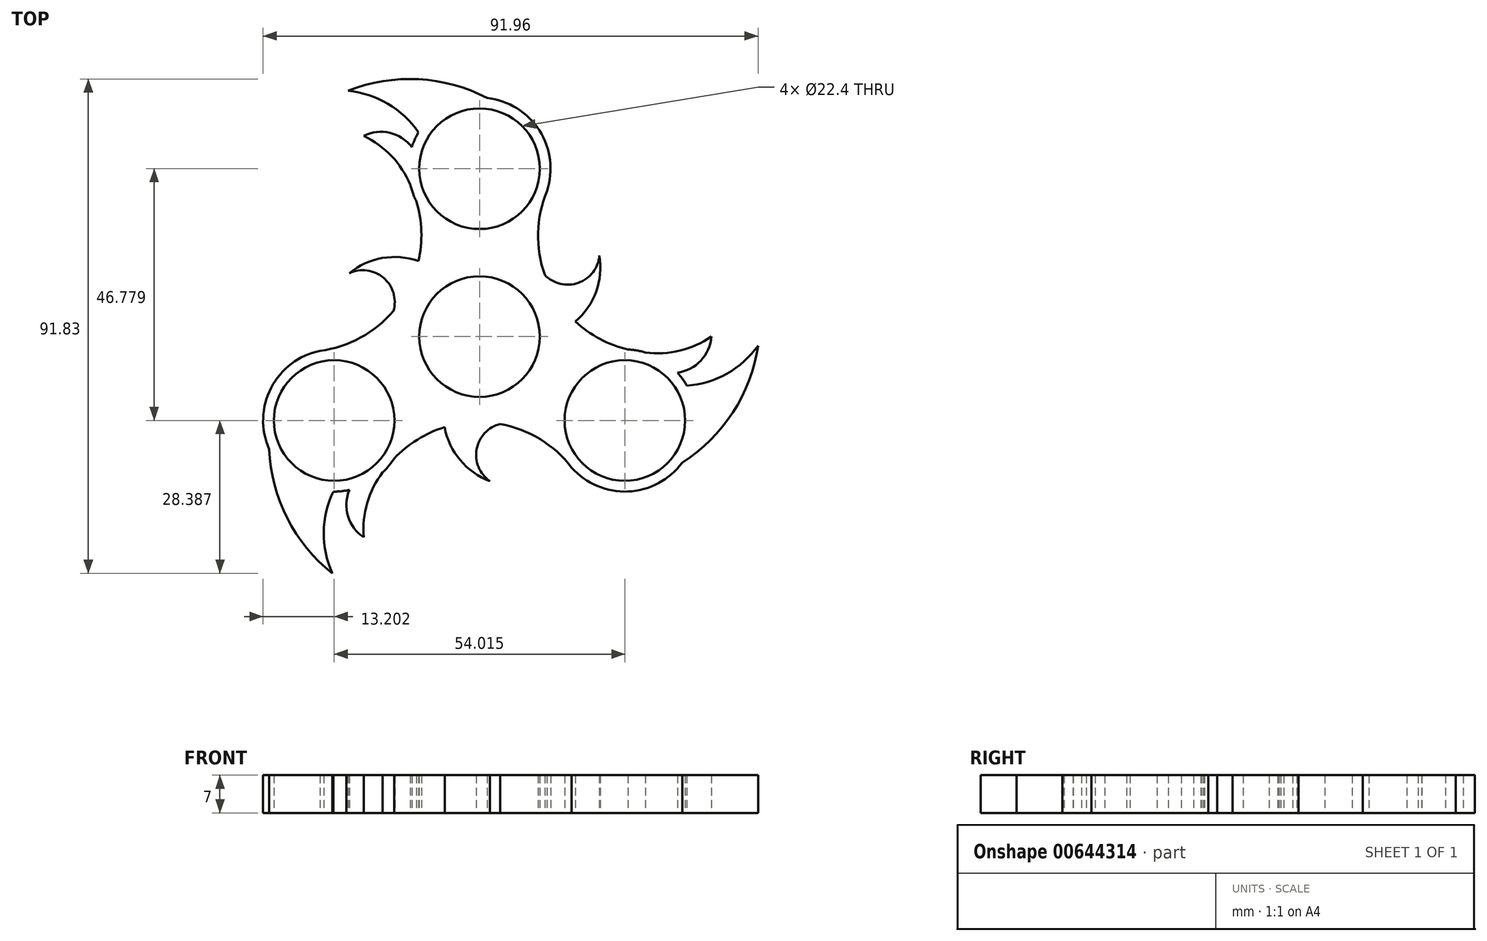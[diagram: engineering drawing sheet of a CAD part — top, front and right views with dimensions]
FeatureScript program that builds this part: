
annotation { "Feature Type Name" : "Feature", "Feature Type Description" : "" }
export const myFeature = defineFeature(function(context is Context, id is Id, definition is map)
    precondition{}
    {
        {
            var Q0;
            Q0=qCreatedBy(makeId("Top.planeOp"),FACE);
            var sketch = newSketch(context, id + "F0", { "sketchPlane" : qUnion([Q0])});
            skCircle(sketch, "E0", {"center": v(0, 0) * mm, "radius": 11.2 * mm});
            skCircle(sketch, "E1", {"center": v(0, 31.19) * mm, "radius": 11.2 * mm});
            skArc(sketch, "E2", {"start": v(12.11, 25.94) * mm, "mid": v(11.4, 37.82) * mm, "end": v(1.43, 44.3) * mm});
            skArc(sketch, "E3.1.0", {"start": v(-17.98, -25.22) * mm, "mid": v(-16.84, -24.01) * mm, "end": v(-15.87, -22.67) * mm});
            skCircle(sketch, "E3.1.1", {"center": v(-27, -15.6) * mm, "radius": 11.2 * mm});
            skArc(sketch, "E3.2.0", {"start": v(38.52, -9.13) * mm, "mid": v(37.71, -7.87) * mm, "end": v(36.77, -6.7) * mm});
            skCircle(sketch, "E3.2.1", {"center": v(27, -15.6) * mm, "radius": 11.2 * mm});
            skArc(sketch, "E4", {"start": v(37.66, -23.4) * mm, "mid": v(47.08, -14.08) * mm, "end": v(51.75, -1.68) * mm});
            skArc(sketch, "E5", {"start": v(38.52, -9.13) * mm, "mid": v(45.97, -6.88) * mm, "end": v(51.75, -1.68) * mm});
            skArc(sketch, "E6", {"start": v(36.77, -6.7) * mm, "mid": v(41.11, -4.48) * mm, "end": v(43.06, 0) * mm});
            skArc(sketch, "E7", {"start": v(30.84, -2.96) * mm, "mid": v(37.22, -2.6) * mm, "end": v(43.06, 0) * mm});
            skArc(sketch, "E8.1.0", {"start": v(1.43, 44.3) * mm, "mid": v(-11.35, 47.8) * mm, "end": v(-24.42, 45.66) * mm});
            skArc(sketch, "E8.2.0", {"start": v(-39.09, -20.92) * mm, "mid": v(-35.73, -33.73) * mm, "end": v(-27.33, -43.98) * mm});
            skArc(sketch, "E9.1.0", {"start": v(-11.35, 37.93) * mm, "mid": v(-17.03, 43.25) * mm, "end": v(-24.42, 45.66) * mm});
            skArc(sketch, "E9.1.2", {"start": v(-12.58, 35.2) * mm, "mid": v(-16.68, 37.84) * mm, "end": v(-21.53, 37.29) * mm});
            skArc(sketch, "E9.1.3", {"start": v(-12.85, 28.18) * mm, "mid": v(-16.35, 33.54) * mm, "end": v(-21.53, 37.29) * mm});
            skArc(sketch, "E9.2.0", {"start": v(-27.17, -28.8) * mm, "mid": v(-28.94, -36.37) * mm, "end": v(-27.33, -43.98) * mm});
            skArc(sketch, "E9.2.2", {"start": v(-24.19, -28.49) * mm, "mid": v(-24.43, -33.36) * mm, "end": v(-21.53, -37.29) * mm});
            skArc(sketch, "E9.2.3", {"start": v(-17.98, -25.22) * mm, "mid": v(-20.87, -30.93) * mm, "end": v(-21.53, -37.29) * mm});
            skArc(sketch, "E10", {"start": v(12.52, 27) * mm, "mid": v(10.88, 19.26) * mm, "end": v(12.12, 11.46) * mm});
            skArc(sketch, "E11.1.0", {"start": v(-29.64, -2.66) * mm, "mid": v(-22.12, -0.2) * mm, "end": v(-15.98, 4.77) * mm});
            skArc(sketch, "E11.2.0", {"start": v(17.12, -24.34) * mm, "mid": v(11.24, -19.06) * mm, "end": v(3.86, -16.23) * mm});
            skArc(sketch, "E12", {"start": v(12.12, 11.46) * mm, "mid": v(18.37, 9.98) * mm, "end": v(22.28, 15.07) * mm});
            skArc(sketch, "E13", {"start": v(17.81, 2.8) * mm, "mid": v(21.67, 8.35) * mm, "end": v(22.28, 15.07) * mm});
            skArc(sketch, "E14.1.0", {"start": v(-15.98, 4.77) * mm, "mid": v(-17.83, 10.92) * mm, "end": v(-24.2, 11.76) * mm});
            skArc(sketch, "E14.1.1", {"start": v(-11.34, 14.03) * mm, "mid": v(-18.06, 14.59) * mm, "end": v(-24.2, 11.76) * mm});
            skArc(sketch, "E14.2.0", {"start": v(3.86, -16.23) * mm, "mid": v(-0.54, -20.9) * mm, "end": v(1.91, -26.83) * mm});
            skArc(sketch, "E14.2.1", {"start": v(-6.48, -16.83) * mm, "mid": v(-3.6, -22.94) * mm, "end": v(1.91, -26.83) * mm});
            skArc(sketch, "E15.trimOffspring", {"start": v(-11.35, 37.93) * mm, "mid": v(-12.04, 36.6) * mm, "end": v(-12.58, 35.2) * mm});
            skArc(sketch, "E16.trimOffspring", {"start": v(-12.85, 28.18) * mm, "mid": v(-12.38, 26.6) * mm, "end": v(-11.7, 25.08) * mm});
            skArc(sketch, "E17.trimOffspring", {"start": v(-27.17, -28.8) * mm, "mid": v(-25.67, -28.72) * mm, "end": v(-24.19, -28.49) * mm});
            skArc(sketch, "E18.trimOffspring", {"start": v(30.84, -2.96) * mm, "mid": v(29.22, -2.58) * mm, "end": v(27.57, -2.4) * mm});
            skArc(sketch, "E19.trimOffspring", {"start": v(17.81, 2.8) * mm, "mid": v(22.35, -0.43) * mm, "end": v(27.57, -2.4) * mm});
            skArc(sketch, "E20.trimOffspring", {"start": v(-11.34, 14.03) * mm, "mid": v(-10.8, 19.57) * mm, "end": v(-11.7, 25.08) * mm});
            skArc(sketch, "E21.trimOffspring", {"start": v(-6.48, -16.83) * mm, "mid": v(-11.55, -19.14) * mm, "end": v(-15.87, -22.67) * mm});
            skArc(sketch, "E22.trimOffspring", {"start": v(-28.52, -2.48) * mm, "mid": v(-38.46, -9.03) * mm, "end": v(-39.09, -20.92) * mm});
            skArc(sketch, "E23.trimOffspring", {"start": v(16.41, -23.46) * mm, "mid": v(27.05, -28.8) * mm, "end": v(37.66, -23.4) * mm});
            skSolve(sketch);
        }
        {
            var Q0;
            Q0=makeQuery(id+"F0.imprint","IMPRINT",FACE,{"disambiguationData":[TD([[makeQuery(id+"F0.imprint","IMPRINT",EDGE,{"derivedFrom":sQuery(id+"F0.wireOp",EDGE,"E0")}),-1.0]])]});
            extrude(context, id + "F1", {"entities" : qUnion([Q0]), "depth" : 7 * mm, "offsetDistance" : 25 * mm});
        }
    });
